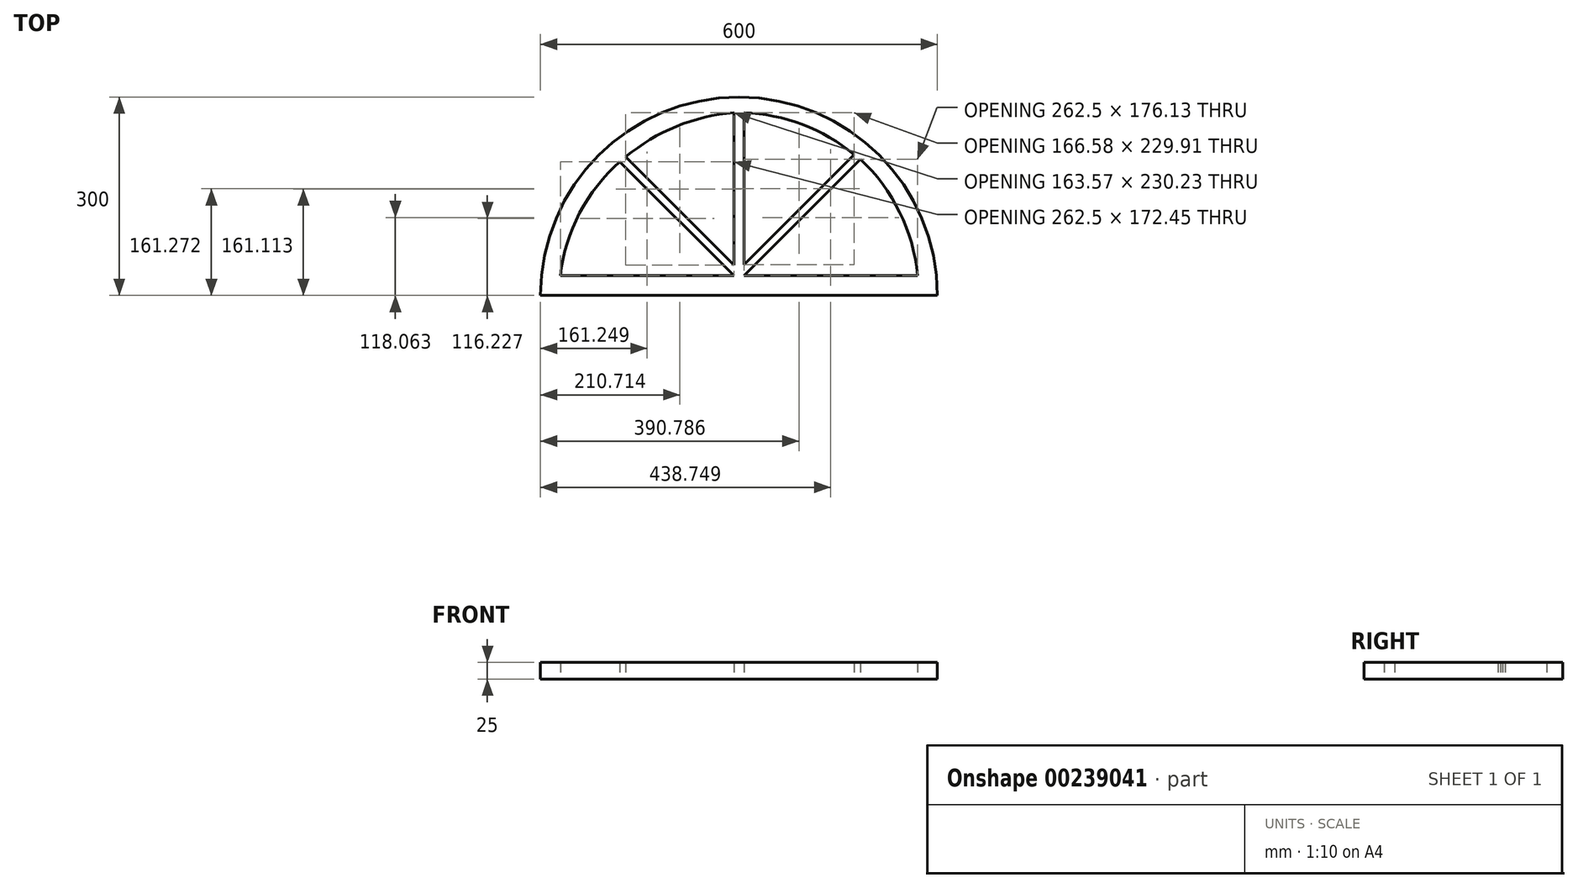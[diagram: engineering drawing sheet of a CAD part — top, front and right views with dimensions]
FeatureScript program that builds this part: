
annotation { "Feature Type Name" : "Feature", "Feature Type Description" : "" }
export const myFeature = defineFeature(function(context is Context, id is Id, definition is map)
    precondition{}
    {
        {
            var Q0;
            Q0=qCreatedBy(makeId("Top.planeOp"),FACE);
            var sketch = newSketch(context, id + "F0", { "sketchPlane" : qUnion([Q0])});
            skLineSegment(sketch, "E0", {"start": v(343.76, -247.18) * mm, "end": v(-256.24, -247.18) * mm});
            skArc(sketch, "E1", {"start": v(343.76, -247.18) * mm, "mid": v(43.76, 52.82) * mm, "end": v(-256.24, -247.18) * mm});
            skLineSegment(sketch, "E2", {"start": v(36.26, -217.18) * mm, "end": v(-226.24, -217.18) * mm});
            skLineSegment(sketch, "E3", {"start": v(51.26, -217.18) * mm, "end": v(313.76, -217.18) * mm});
            skLineSegment(sketch, "E4", {"start": v(36.26, -217.18) * mm, "end": v(-136.2, -44.73) * mm});
            skArc(sketch, "E5", {"start": v(-136.2, -44.73) * mm, "mid": v(-197.22, -122.6) * mm, "end": v(-226.24, -217.18) * mm});
            skLineSegment(sketch, "E6", {"start": v(51.26, -217.18) * mm, "end": v(227.38, -41.05) * mm});
            skArc(sketch, "E7", {"start": v(313.76, -217.18) * mm, "mid": v(286.68, -121.22) * mm, "end": v(227.38, -41.05) * mm});
            skLineSegment(sketch, "E8", {"start": v(51.26, -200.86) * mm, "end": v(217.83, -34.29) * mm});
            skLineSegment(sketch, "E9", {"start": v(36.26, -201.18) * mm, "end": v(-127.31, -37.61) * mm});
            skLineSegment(sketch, "E10", {"start": v(36.26, -201.18) * mm, "end": v(36.26, 29.05) * mm});
            skLineSegment(sketch, "E11", {"start": v(51.26, -200.86) * mm, "end": v(51.26, 29.05) * mm});
            skArc(sketch, "E12", {"start": v(36.26, 29.05) * mm, "mid": v(-50.78, 8.6) * mm, "end": v(-127.31, -37.61) * mm});
            skArc(sketch, "E13", {"start": v(217.83, -34.29) * mm, "mid": v(139.85, 11.34) * mm, "end": v(51.26, 29.05) * mm});
            skSolve(sketch);
        }
        {
            var Q0;
            Q0=makeQuery(id+"F0.imprint","IMPRINT",FACE,{"disambiguationData":[TD([[makeQuery(id+"F0.imprint","IMPRINT",EDGE,{"derivedFrom":sQuery(id+"F0.wireOp",EDGE,"E0")}),-1.0]])]});
            extrude(context, id + "F1", {"entities" : qUnion([Q0]), "depth" : 25 * mm});
        }
    });
